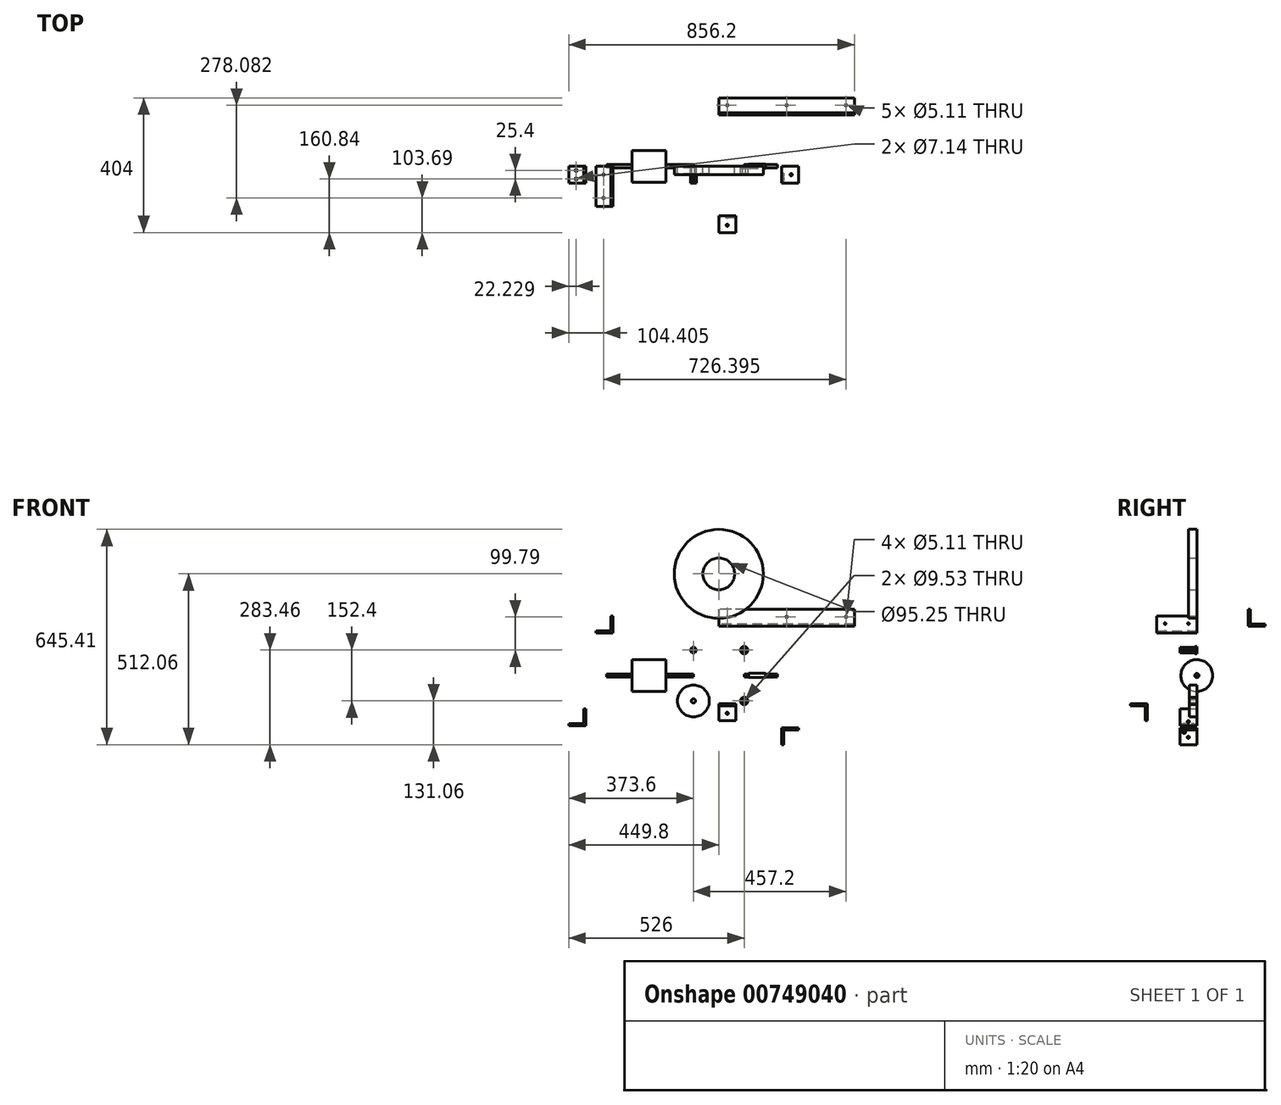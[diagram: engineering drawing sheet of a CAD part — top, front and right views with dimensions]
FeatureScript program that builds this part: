
annotation { "Feature Type Name" : "Feature", "Feature Type Description" : "" }
export const myFeature = defineFeature(function(context is Context, id is Id, definition is map)
    precondition{}
    {
        {
            var Q0;
            Q0=qCreatedBy(makeId("Front.planeOp"),FACE);
            var sketch = newSketch(context, id + "F0", { "sketchPlane" : qUnion([Q0])});
            skCircle(sketch, "E0.cCircle", {"center": v(-76.2, 76.2) * mm, "radius": 7.94 * mm, "construction": true});
            skLineSegment(sketch, "E0.0", {"start": v(-67.03, 76.2) * mm, "end": v(-71.62, 68.26) * mm});
            skLineSegment(sketch, "E0.1", {"start": v(-71.62, 68.26) * mm, "end": v(-80.78, 68.26) * mm});
            skLineSegment(sketch, "E0.2", {"start": v(-80.78, 68.26) * mm, "end": v(-85.37, 76.2) * mm});
            skLineSegment(sketch, "E0.3", {"start": v(-85.37, 76.2) * mm, "end": v(-80.78, 84.14) * mm});
            skLineSegment(sketch, "E0.4", {"start": v(-80.78, 84.14) * mm, "end": v(-71.62, 84.14) * mm});
            skLineSegment(sketch, "E0.5", {"start": v(-71.62, 84.14) * mm, "end": v(-67.03, 76.2) * mm});
            skPoint(sketch, "E0.0.midPoint", {"position": v(-69.33, 72.23) * mm});
            skSolve(sketch);
        }
        {
            var Q0;
            Q0 = qSketchRegion(id + "F0", true);
            extrude(context, id + "F1", {"entities" : qUnion([Q0]), "depth" : 50.8 * mm, "offsetDistance" : 25.4 * mm});
        }
        {
            var Q0;
            Q0=sQuery(id+"F0.wireOp",VERTEX,"E0.cCircle.center");
            var Q1;
            Q1=makeQuery(id+"F1.opExtrude","SWEPT_BODY",BODY,{"disambiguationData":[OSD([sQuery(id+"F0.wireOp",EDGE,"E0.0"),sQuery(id+"F0.wireOp",EDGE,"E0.1"),sQuery(id+"F0.wireOp",EDGE,"E0.2"),sQuery(id+"F0.wireOp",EDGE,"E0.3"),sQuery(id+"F0.wireOp",EDGE,"E0.4"),sQuery(id+"F0.wireOp",EDGE,"E0.5")])]});
            hole(context, id + "F2", {"style" : HoleStyle.SIMPLE, "endStyle" : HoleEndStyle.THROUGH, "oppositeDirection" : true, "standardTappedOrClearance" : lookupTablePath({ "standard" : "ANSI", "engagement" : "75%", "pitch" : "20 tpi", "size" : "1/4", "type" : "Tapped" }), "standardBlindInLast" : lookupTablePath({ "standard" : "ANSI", "fit" : "Normal", "engagement" : "75%", "pitch" : "20 tpi", "size" : "1/4", "type" : "Clearance & tapped" }), "holeDiameter" : 5.1 * mm, "majorDiameter" : 6.35 * mm, "showTappedDepth" : true, "isTappedThrough" : true, "tappedDepth" : 22.25 * mm, "tapClearance" : 3, "locations" : qUnion([Q0]), "scope" : qUnion([Q1])});
        }
        {
            var Q0;
            Q0=qCreatedBy(makeId("Front.planeOp"),FACE);
            var sketch = newSketch(context, id + "F3", { "sketchPlane" : qUnion([Q0])});
            skCircle(sketch, "E1", {"center": v(76.2, 76.2) * mm, "radius": 4.76 * mm});
            skCircle(sketch, "E2", {"center": v(76.2, 76.2) * mm, "radius": 11.11 * mm});
            skSolve(sketch);
        }
        {
            var Q0;
            Q0 = qSketchRegion(id + "F3", true);
            extrude(context, id + "F4", {"entities" : qUnion([Q0]), "depth" : 6.35 * mm, "offsetDistance" : 25.4 * mm});
        }
        {
            var Q0;
            Q0=qCreatedBy(makeId("Front.planeOp"),FACE);
            var sketch = newSketch(context, id + "F5", { "sketchPlane" : qUnion([Q0])});
            skLineSegment(sketch, "E3", {"start": v(76.2, 0) * mm, "end": v(76.2, 4.76) * mm});
            skLineSegment(sketch, "E4", {"start": v(76.2, 4.76) * mm, "end": v(88.9, 4.76) * mm});
            skLineSegment(sketch, "E5", {"start": v(88.9, 4.76) * mm, "end": v(88.9, 6.35) * mm});
            skLineSegment(sketch, "E6", {"start": v(88.9, 6.35) * mm, "end": v(139.7, 6.35) * mm});
            skLineSegment(sketch, "E7", {"start": v(139.7, 6.35) * mm, "end": v(139.7, 4.76) * mm});
            skLineSegment(sketch, "E8", {"start": v(139.7, 4.76) * mm, "end": v(176.21, 4.76) * mm});
            skLineSegment(sketch, "E9", {"start": v(176.21, 4.76) * mm, "end": v(176.21, 0) * mm});
            skLineSegment(sketch, "E10", {"start": v(176.21, 0) * mm, "end": v(76.2, 0) * mm});
            skSolve(sketch);
        }
        {
            var Q0;
            Q0 = qSketchRegion(id + "F5", true);
            var Q1;
            Q1=sQuery(id+"F5.wireOp",EDGE,"E10");
            revolve(context, id + "F6", {"surfaceOperationType" : NewSurfaceOperationType.NEW, "entities" : qUnion([Q0]), "axis" : qUnion([Q1]), "revolveType" : RevolveType.FULL});
        }
        {
            var Q0;
            Q0=qCreatedBy(makeId("Front.planeOp"),FACE);
            var sketch = newSketch(context, id + "F7", { "sketchPlane" : qUnion([Q0])});
            skCircle(sketch, "E11", {"center": v(-76.2, -76.2) * mm, "radius": 47.75 * mm});
            skCircle(sketch, "E12", {"center": v(-76.2, -76.2) * mm, "radius": 6.35 * mm});
            skSolve(sketch);
        }
        {
            var Q0;
            Q0=makeQuery(id+"F7.imprint","IMPRINT",FACE,{"disambiguationData":[TD([[makeQuery(id+"F7.imprint","IMPRINT",EDGE,{"derivedFrom":sQuery(id+"F7.wireOp",EDGE,"E11")}),1.0]])]});
            extrude(context, id + "F8", {"entities" : qUnion([Q0]), "depth" : 22.22 * mm, "offsetDistance" : 25.4 * mm});
        }
        {
            var Q0;
            Q0=qCreatedBy(makeId("Front.planeOp"),FACE);
            var sketch = newSketch(context, id + "F9", { "sketchPlane" : qUnion([Q0])});
            skCircle(sketch, "E13", {"center": v(76.2, -76.2) * mm, "radius": 11.14 * mm});
            skCircle(sketch, "E14", {"center": v(76.2, -76.2) * mm, "radius": 4.76 * mm});
            skSolve(sketch);
        }
        {
            var Q0;
            Q0 = qSketchRegion(id + "F9", true);
            extrude(context, id + "F10", {"entities" : qUnion([Q0]), "depth" : 22.22 * mm, "offsetDistance" : 25.4 * mm});
        }
        {
            var Q0;
            Q0=qCreatedBy(makeId("Front.planeOp"),FACE);
            var sketch = newSketch(context, id + "F11", { "sketchPlane" : qUnion([Q0])});
            skLineSegment(sketch, "E15", {"start": v(-76.2, 0) * mm, "end": v(-76.2, 4.76) * mm});
            skLineSegment(sketch, "E16", {"start": v(-76.2, 4.76) * mm, "end": v(-158.75, 4.76) * mm});
            skLineSegment(sketch, "E17", {"start": v(-158.75, 4.76) * mm, "end": v(-158.75, 47.63) * mm});
            skLineSegment(sketch, "E18", {"start": v(-158.75, 47.63) * mm, "end": v(-260.35, 47.62) * mm});
            skLineSegment(sketch, "E19", {"start": v(-260.35, 47.62) * mm, "end": v(-260.35, 4.76) * mm});
            skLineSegment(sketch, "E20", {"start": v(-260.35, 4.76) * mm, "end": v(-336.55, 4.76) * mm});
            skLineSegment(sketch, "E21", {"start": v(-336.55, 4.76) * mm, "end": v(-336.55, 0) * mm});
            skLineSegment(sketch, "E22", {"start": v(-336.55, 0) * mm, "end": v(-76.2, 0) * mm});
            skSolve(sketch);
        }
        {
            var Q0;
            Q0=makeQuery(id+"F11.imprint","IMPRINT",FACE,{"disambiguationData":[TD([[makeQuery(id+"F11.imprint","IMPRINT",EDGE,{"derivedFrom":sQuery(id+"F11.wireOp",EDGE,"E15")}),1.0]])]});
            var Q1;
            Q1=sQuery(id+"F11.wireOp",EDGE,"E22");
            revolve(context, id + "F12", {"surfaceOperationType" : NewSurfaceOperationType.NEW, "entities" : qUnion([Q0]), "axis" : qUnion([Q1]), "revolveType" : RevolveType.FULL});
        }
        {
            var Q0;
            Q0=qCreatedBy(makeId("Front.planeOp"),FACE);
            var sketch = newSketch(context, id + "F13", { "sketchPlane" : qUnion([Q0])});
            skCircle(sketch, "E23", {"center": v(0, 304.8) * mm, "radius": 133.35 * mm});
            skCircle(sketch, "E24", {"center": v(0, 304.8) * mm, "radius": 47.63 * mm});
            skSolve(sketch);
        }
        {
            var Q0;
            Q0 = qSketchRegion(id + "F13", true);
            extrude(context, id + "F14", {"entities" : qUnion([Q0]), "depth" : 25.4 * mm, "offsetDistance" : 25.4 * mm});
        }
        {
            var Q0;
            Q0=qCreatedBy(makeId("Front.planeOp"),FACE);
            var sketch = newSketch(context, id + "F15", { "sketchPlane" : qUnion([Q0])});
            skLineSegment(sketch, "E25", {"start": v(-367.62, 127.11) * mm, "end": v(-316.82, 127.11) * mm});
            skLineSegment(sketch, "E26", {"start": v(-316.82, 127.11) * mm, "end": v(-316.82, 177.91) * mm});
            skLineSegment(sketch, "E27", {"start": v(-316.82, 177.91) * mm, "end": v(-323.17, 177.91) * mm});
            skLineSegment(sketch, "E28", {"start": v(-323.17, 177.91) * mm, "end": v(-323.17, 133.46) * mm});
            skLineSegment(sketch, "E29", {"start": v(-323.17, 133.46) * mm, "end": v(-367.62, 133.46) * mm});
            skLineSegment(sketch, "E30", {"start": v(-367.62, 133.46) * mm, "end": v(-367.62, 127.11) * mm});
            skSolve(sketch);
        }
        {
            var Q0;
            Q0 = qSketchRegion(id + "F15", true);
            extrude(context, id + "F16", {"entities" : qUnion([Q0]), "depth" : 120.65 * mm, "offsetDistance" : 25.4 * mm});
        }
        {
            var Q0;
            Q0=makeQuery(id+"F16.opExtrude","SWEPT_FACE",FACE,{"disambiguationData":[OSD([sQuery(id+"F15.wireOp",EDGE,"E29")])]});
            var sketch = newSketch(context, id + "F17", { "sketchPlane" : qUnion([Q0])});
            skLineSegment(sketch, "E31", {"start": v(-345.4, 0) * mm, "end": v(-345.4, -120.65) * mm, "construction": true});
            skPoint(sketch, "E32", {"position": v(-345.4, -25.4) * mm});
            skPoint(sketch, "E33", {"position": v(-345.4, -95.25) * mm});
            skSolve(sketch);
        }
        {
            var Q0;
            Q0=makeQuery(id+"F16.opExtrude","SWEPT_FACE",FACE,{"disambiguationData":[OSD([sQuery(id+"F15.wireOp",EDGE,"E28")])]});
            var sketch = newSketch(context, id + "F18", { "sketchPlane" : qUnion([Q0])});
            skLineSegment(sketch, "E34", {"start": v(0, 155.69) * mm, "end": v(120.65, 155.69) * mm, "construction": true});
            skPoint(sketch, "E35", {"position": v(25.4, 155.69) * mm});
            skPoint(sketch, "E36", {"position": v(95.25, 155.69) * mm});
            skSolve(sketch);
        }
        {
            var Q0;
            Q0=sQuery(id+"F18.wireOp",VERTEX,"E36");
            var Q1;
            Q1=sQuery(id+"F18.wireOp",VERTEX,"E35");
            var Q2;
            Q2=sQuery(id+"F17.wireOp",VERTEX,"E33");
            var Q3;
            Q3=sQuery(id+"F17.wireOp",VERTEX,"E32");
            var Q4;
            Q4=makeQuery(id+"F16.opExtrude","SWEPT_BODY",BODY,{"disambiguationData":[OSD([sQuery(id+"F15.wireOp",EDGE,"E25"),sQuery(id+"F15.wireOp",EDGE,"E26"),sQuery(id+"F15.wireOp",EDGE,"E27"),sQuery(id+"F15.wireOp",EDGE,"E28"),sQuery(id+"F15.wireOp",EDGE,"E29"),sQuery(id+"F15.wireOp",EDGE,"E30")])]});
            hole(context, id + "F19", {"style" : HoleStyle.SIMPLE, "endStyle" : HoleEndStyle.THROUGH, "standardTappedOrClearance" : lookupTablePath({ "standard" : "ANSI", "engagement" : "75%", "pitch" : "20 tpi", "size" : "1/4", "type" : "Tapped" }), "standardBlindInLast" : lookupTablePath({ "standard" : "ANSI", "fit" : "Free", "engagement" : "75%", "pitch" : "20 tpi", "size" : "1/4", "type" : "Clearance & tapped" }), "holeDiameter" : 5.1 * mm, "majorDiameter" : 6.35 * mm, "showTappedDepth" : true, "isTappedThrough" : true, "tappedDepth" : 22.25 * mm, "tapClearance" : 3, "locations" : qUnion([Q0, Q1, Q2, Q3]), "scope" : qUnion([Q4])});
        }
        {
            var Q0;
            Q0=qCreatedBy(makeId("Right.planeOp"),FACE);
            var sketch = newSketch(context, id + "F20", { "sketchPlane" : qUnion([Q0])});
            skLineSegment(sketch, "E37", {"start": v(205.06, 147.41) * mm, "end": v(154.26, 147.41) * mm});
            skLineSegment(sketch, "E38", {"start": v(154.26, 147.41) * mm, "end": v(154.26, 198.21) * mm});
            skLineSegment(sketch, "E39", {"start": v(154.26, 198.21) * mm, "end": v(160.6, 198.21) * mm});
            skLineSegment(sketch, "E40", {"start": v(160.6, 198.21) * mm, "end": v(160.6, 153.76) * mm});
            skLineSegment(sketch, "E41", {"start": v(160.6, 153.76) * mm, "end": v(205.06, 153.76) * mm});
            skLineSegment(sketch, "E42", {"start": v(205.06, 153.76) * mm, "end": v(205.06, 147.41) * mm});
            skSolve(sketch);
        }
        {
            var Q0;
            Q0 = qSketchRegion(id + "F20", true);
            extrude(context, id + "F21", {"entities" : qUnion([Q0]), "depth" : 406.4 * mm, "offsetDistance" : 25.4 * mm});
        }
        {
            var Q0;
            Q0=makeQuery(id+"F21.opExtrude","SWEPT_FACE",FACE,{"disambiguationData":[OSD([sQuery(id+"F20.wireOp",EDGE,"E41")])]});
            var sketch = newSketch(context, id + "F22", { "sketchPlane" : qUnion([Q0])});
            skLineSegment(sketch, "E43", {"start": v(406.4, 182.83) * mm, "end": v(0, 182.83) * mm, "construction": true});
            skPoint(sketch, "E44", {"position": v(381, 182.83) * mm});
            skPoint(sketch, "E45", {"position": v(203.2, 182.83) * mm});
            skPoint(sketch, "E46", {"position": v(25.4, 182.83) * mm});
            skSolve(sketch);
        }
        {
            var Q0;
            Q0=makeQuery(id+"F21.opExtrude","SWEPT_FACE",FACE,{"disambiguationData":[OSD([sQuery(id+"F20.wireOp",EDGE,"E40")])]});
            var sketch = newSketch(context, id + "F23", { "sketchPlane" : qUnion([Q0])});
            skLineSegment(sketch, "E47", {"start": v(-406.4, 175.99) * mm, "end": v(0, 175.99) * mm, "construction": true});
            skPoint(sketch, "E48", {"position": v(-203.2, 175.99) * mm});
            skPoint(sketch, "E49", {"position": v(-381, 175.99) * mm});
            skPoint(sketch, "E50", {"position": v(-25.4, 175.99) * mm});
            skSolve(sketch);
        }
        {
            var Q0;
            Q0=sQuery(id+"F23.wireOp",VERTEX,"E50");
            var Q1;
            Q1=sQuery(id+"F23.wireOp",VERTEX,"E48");
            var Q2;
            Q2=sQuery(id+"F23.wireOp",VERTEX,"E49");
            var Q3;
            Q3=sQuery(id+"F22.wireOp",VERTEX,"E44");
            var Q4;
            Q4=sQuery(id+"F22.wireOp",VERTEX,"E45");
            var Q5;
            Q5=sQuery(id+"F22.wireOp",VERTEX,"E46");
            var Q6;
            Q6=makeQuery(id+"F14.opExtrude","SWEPT_BODY",BODY,{"disambiguationData":[OSD([sQuery(id+"F13.wireOp",EDGE,"E23"),sQuery(id+"F13.wireOp",EDGE,"E24")])]});
            var Q7;
            Q7=makeQuery(id+"F21.opExtrude","SWEPT_BODY",BODY,{"disambiguationData":[OSD([sQuery(id+"F20.wireOp",EDGE,"E37"),sQuery(id+"F20.wireOp",EDGE,"E38"),sQuery(id+"F20.wireOp",EDGE,"E39"),sQuery(id+"F20.wireOp",EDGE,"E40"),sQuery(id+"F20.wireOp",EDGE,"E41"),sQuery(id+"F20.wireOp",EDGE,"E42")])]});
            hole(context, id + "F24", {"style" : HoleStyle.SIMPLE, "endStyle" : HoleEndStyle.BLIND, "standardTappedOrClearance" : lookupTablePath({ "standard" : "ANSI", "engagement" : "75%", "pitch" : "20 tpi", "size" : "1/4", "type" : "Tapped" }), "standardBlindInLast" : lookupTablePath({ "standard" : "ANSI", "fit" : "Free", "engagement" : "75%", "pitch" : "20 tpi", "size" : "1/4", "type" : "Clearance & tapped" }), "holeDiameter" : 5.1 * mm, "majorDiameter" : 6.35 * mm, "showTappedDepth" : true, "holeDepth" : 10.26 * mm, "tappedDepth" : 6.45 * mm, "tapClearance" : 3, "locations" : qUnion([Q0, Q1, Q2, Q3, Q4, Q5]), "scope" : qUnion([Q6, Q7])});
        }
        {
            var Q0;
            Q0=qCreatedBy(makeId("Front.planeOp"),FACE);
            var sketch = newSketch(context, id + "F25", { "sketchPlane" : qUnion([Q0])});
            skLineSegment(sketch, "E51", {"start": v(188.28, -207.26) * mm, "end": v(188.28, -156.46) * mm});
            skLineSegment(sketch, "E52", {"start": v(188.28, -156.46) * mm, "end": v(239.08, -156.46) * mm});
            skLineSegment(sketch, "E53", {"start": v(239.08, -156.46) * mm, "end": v(239.08, -162.8) * mm});
            skLineSegment(sketch, "E54", {"start": v(239.08, -162.8) * mm, "end": v(194.63, -162.8) * mm});
            skLineSegment(sketch, "E55", {"start": v(194.63, -162.8) * mm, "end": v(194.63, -207.26) * mm});
            skLineSegment(sketch, "E56", {"start": v(194.63, -207.26) * mm, "end": v(188.28, -207.26) * mm});
            skSolve(sketch);
        }
        {
            var Q0;
            Q0 = qSketchRegion(id + "F25", true);
            extrude(context, id + "F26", {"entities" : qUnion([Q0]), "depth" : 50.8 * mm, "offsetDistance" : 25.4 * mm});
        }
        {
            var Q0;
            Q0=makeQuery(id+"F26.opExtrude","SWEPT_FACE",FACE,{"disambiguationData":[OSD([sQuery(id+"F25.wireOp",EDGE,"E55")])]});
            var sketch = newSketch(context, id + "F27", { "sketchPlane" : qUnion([Q0])});
            skLineSegment(sketch, "E57", {"start": v(-50.8, -185.03) * mm, "end": v(0, -185.03) * mm, "construction": true});
            skPoint(sketch, "E58", {"position": v(-25.4, -185.03) * mm});
            skPoint(sketch, "E59", {"position": v(-38.1, -169.16) * mm});
            skSolve(sketch);
        }
        {
            var Q0;
            Q0=makeQuery(id+"F26.opExtrude","SWEPT_FACE",FACE,{"disambiguationData":[OSD([sQuery(id+"F25.wireOp",EDGE,"E54")])]});
            var sketch = newSketch(context, id + "F28", { "sketchPlane" : qUnion([Q0])});
            skLineSegment(sketch, "E60", {"start": v(216.86, 50.8) * mm, "end": v(216.86, 0) * mm, "construction": true});
            skPoint(sketch, "E61", {"position": v(216.86, 25.4) * mm});
            skSolve(sketch);
        }
        {
            var Q0;
            Q0=sQuery(id+"F28.wireOp",VERTEX,"E61");
            var Q1;
            Q1=sQuery(id+"F27.wireOp",VERTEX,"E58");
            var Q2;
            Q2=makeQuery(id+"F26.opExtrude","SWEPT_BODY",BODY,{"disambiguationData":[OSD([sQuery(id+"F25.wireOp",EDGE,"E51"),sQuery(id+"F25.wireOp",EDGE,"E52"),sQuery(id+"F25.wireOp",EDGE,"E53"),sQuery(id+"F25.wireOp",EDGE,"E54"),sQuery(id+"F25.wireOp",EDGE,"E55"),sQuery(id+"F25.wireOp",EDGE,"E56")])]});
            hole(context, id + "F29", {"style" : HoleStyle.SIMPLE, "endStyle" : HoleEndStyle.THROUGH, "standardTappedOrClearance" : lookupTablePath({ "fit" : "Free", "standard" : "ANSI", "size" : "1/4", "type" : "Clearance" }), "standardBlindInLast" : lookupTablePath({ "fit" : "Free", "standard" : "ANSI", "engagement" : "75%", "pitch" : "20 tpi", "size" : "1/4", "type" : "Clearance & tapped" }), "holeDiameter" : 6.76 * mm, "majorDiameter" : 6.35 * mm, "isTappedThrough" : true, "tappedDepth" : 22.25 * mm, "tapClearance" : 3, "locations" : qUnion([Q0, Q1]), "scope" : qUnion([Q2])});
        }
        {
            var Q0;
            Q0=sQuery(id+"F27.wireOp",VERTEX,"E59");
            var Q1;
            Q1=makeQuery(id+"F26.opExtrude","SWEPT_BODY",BODY,{"disambiguationData":[OSD([sQuery(id+"F25.wireOp",EDGE,"E51"),sQuery(id+"F25.wireOp",EDGE,"E52"),sQuery(id+"F25.wireOp",EDGE,"E53"),sQuery(id+"F25.wireOp",EDGE,"E54"),sQuery(id+"F25.wireOp",EDGE,"E55"),sQuery(id+"F25.wireOp",EDGE,"E56")])]});
            hole(context, id + "F30", {"style" : HoleStyle.SIMPLE, "endStyle" : HoleEndStyle.THROUGH, "holeDiameter" : 9.52 * mm, "majorDiameter" : 6.35 * mm, "isTappedThrough" : true, "tappedDepth" : 22.25 * mm, "tapClearance" : 3, "locations" : qUnion([Q0]), "scope" : qUnion([Q1])});
        }
        {
            var Q0;
            Q0=qCreatedBy(makeId("Right.planeOp"),FACE);
            var sketch = newSketch(context, id + "F31", { "sketchPlane" : qUnion([Q0])});
            skLineSegment(sketch, "E62", {"start": v(-148.14, -135.62) * mm, "end": v(-148.14, -84.82) * mm});
            skLineSegment(sketch, "E63", {"start": v(-148.14, -84.82) * mm, "end": v(-198.94, -84.82) * mm});
            skLineSegment(sketch, "E64", {"start": v(-198.94, -84.82) * mm, "end": v(-198.94, -91.17) * mm});
            skLineSegment(sketch, "E65", {"start": v(-198.94, -91.17) * mm, "end": v(-154.49, -91.17) * mm});
            skLineSegment(sketch, "E66", {"start": v(-154.49, -91.17) * mm, "end": v(-154.49, -135.62) * mm});
            skLineSegment(sketch, "E67", {"start": v(-154.49, -135.62) * mm, "end": v(-148.14, -135.62) * mm});
            skSolve(sketch);
        }
        {
            var Q0;
            Q0 = qSketchRegion(id + "F31", true);
            extrude(context, id + "F32", {"entities" : qUnion([Q0]), "depth" : 50.8 * mm, "offsetDistance" : 25.4 * mm});
        }
        {
            var Q0;
            Q0=makeQuery(id+"F32.opExtrude","SWEPT_FACE",FACE,{"disambiguationData":[OSD([sQuery(id+"F31.wireOp",EDGE,"E66")])]});
            var sketch = newSketch(context, id + "F33", { "sketchPlane" : qUnion([Q0])});
            skLineSegment(sketch, "E68", {"start": v(0, -113.4) * mm, "end": v(50.8, -113.4) * mm, "construction": true});
            skPoint(sketch, "E69", {"position": v(25.4, -113.4) * mm});
            skSolve(sketch);
        }
        {
            var Q0;
            Q0=makeQuery(id+"F32.opExtrude","SWEPT_FACE",FACE,{"disambiguationData":[OSD([sQuery(id+"F31.wireOp",EDGE,"E65")])]});
            var sketch = newSketch(context, id + "F34", { "sketchPlane" : qUnion([Q0])});
            skLineSegment(sketch, "E70", {"start": v(0, 176.71) * mm, "end": v(50.8, 176.71) * mm, "construction": true});
            skPoint(sketch, "E71", {"position": v(25.4, 176.71) * mm});
            skSolve(sketch);
        }
        {
            var Q0;
            Q0=sQuery(id+"F33.wireOp",VERTEX,"E69");
            var Q1;
            Q1=sQuery(id+"F34.wireOp",VERTEX,"E71");
            var Q2;
            Q2=makeQuery(id+"F32.opExtrude","SWEPT_BODY",BODY,{"disambiguationData":[OSD([sQuery(id+"F31.wireOp",EDGE,"E62"),sQuery(id+"F31.wireOp",EDGE,"E63"),sQuery(id+"F31.wireOp",EDGE,"E64"),sQuery(id+"F31.wireOp",EDGE,"E65"),sQuery(id+"F31.wireOp",EDGE,"E66"),sQuery(id+"F31.wireOp",EDGE,"E67")])]});
            hole(context, id + "F35", {"style" : HoleStyle.SIMPLE, "endStyle" : HoleEndStyle.THROUGH, "standardTappedOrClearance" : lookupTablePath({ "fit" : "Free", "standard" : "ANSI", "size" : "1/4", "type" : "Clearance" }), "standardBlindInLast" : lookupTablePath({ "fit" : "Free", "standard" : "ANSI", "engagement" : "75%", "pitch" : "20 tpi", "size" : "1/4", "type" : "Clearance & tapped" }), "holeDiameter" : 6.76 * mm, "majorDiameter" : 6.35 * mm, "isTappedThrough" : true, "tappedDepth" : 22.25 * mm, "tapClearance" : 3, "locations" : qUnion([Q0, Q1]), "scope" : qUnion([Q2])});
        }
        {
            var Q0;
            Q0=qCreatedBy(makeId("Front.planeOp"),FACE);
            var sketch = newSketch(context, id + "F36", { "sketchPlane" : qUnion([Q0])});
            skLineSegment(sketch, "E72", {"start": v(-449.8, -150.92) * mm, "end": v(-399, -150.92) * mm});
            skLineSegment(sketch, "E73", {"start": v(-399, -150.92) * mm, "end": v(-399, -100.12) * mm});
            skLineSegment(sketch, "E74", {"start": v(-399, -100.12) * mm, "end": v(-405.35, -100.12) * mm});
            skLineSegment(sketch, "E75", {"start": v(-405.35, -100.12) * mm, "end": v(-405.35, -144.57) * mm});
            skLineSegment(sketch, "E76", {"start": v(-405.35, -144.57) * mm, "end": v(-449.8, -144.57) * mm});
            skLineSegment(sketch, "E77", {"start": v(-449.8, -144.57) * mm, "end": v(-449.8, -150.92) * mm});
            skSolve(sketch);
        }
        {
            var Q0;
            Q0 = qSketchRegion(id + "F36", true);
            extrude(context, id + "F37", {"entities" : qUnion([Q0]), "depth" : 50.8 * mm, "offsetDistance" : 25.4 * mm});
        }
        {
            var Q0;
            Q0=makeQuery(id+"F37.opExtrude","SWEPT_FACE",FACE,{"disambiguationData":[OSD([sQuery(id+"F36.wireOp",EDGE,"E76")])]});
            var sketch = newSketch(context, id + "F38", { "sketchPlane" : qUnion([Q0])});
            skLineSegment(sketch, "E78", {"start": v(-427.57, 0) * mm, "end": v(-427.57, -50.8) * mm, "construction": true});
            skPoint(sketch, "E79", {"position": v(-427.57, -12.7) * mm});
            skPoint(sketch, "E80", {"position": v(-427.57, -38.1) * mm});
            skSolve(sketch);
        }
        {
            var Q0;
            Q0=makeQuery(id+"F37.opExtrude","SWEPT_FACE",FACE,{"disambiguationData":[OSD([sQuery(id+"F36.wireOp",EDGE,"E75")])]});
            var sketch = newSketch(context, id + "F39", { "sketchPlane" : qUnion([Q0])});
            skPoint(sketch, "E81", {"position": v(25.4, -138.22) * mm});
            skSolve(sketch);
        }
        {
            var Q0;
            Q0=sQuery(id+"F39.wireOp",VERTEX,"E81");
            var Q1;
            Q1=sQuery(id+"F38.wireOp",VERTEX,"E79");
            var Q2;
            Q2=sQuery(id+"F38.wireOp",VERTEX,"E80");
            var Q3;
            Q3=makeQuery(id+"F37.opExtrude","SWEPT_BODY",BODY,{"disambiguationData":[OSD([sQuery(id+"F36.wireOp",EDGE,"E72"),sQuery(id+"F36.wireOp",EDGE,"E73"),sQuery(id+"F36.wireOp",EDGE,"E74"),sQuery(id+"F36.wireOp",EDGE,"E75"),sQuery(id+"F36.wireOp",EDGE,"E76"),sQuery(id+"F36.wireOp",EDGE,"E77")])]});
            hole(context, id + "F40", {"style" : HoleStyle.SIMPLE, "endStyle" : HoleEndStyle.BLIND, "standardTappedOrClearance" : lookupTablePath({ "fit" : "Normal (ASME)", "standard" : "ANSI", "size" : "1/4", "type" : "Clearance" }), "standardBlindInLast" : lookupTablePath({ "fit" : "Free", "standard" : "ANSI", "engagement" : "75%", "pitch" : "20 tpi", "size" : "1/4", "type" : "Clearance & tapped" }), "holeDiameter" : 7.14 * mm, "majorDiameter" : 6.35 * mm, "holeDepth" : 26.06 * mm, "isTappedThrough" : true, "tappedDepth" : 22.25 * mm, "tapClearance" : 3, "locations" : qUnion([Q0, Q1, Q2]), "scope" : qUnion([Q3])});
        }
    });
